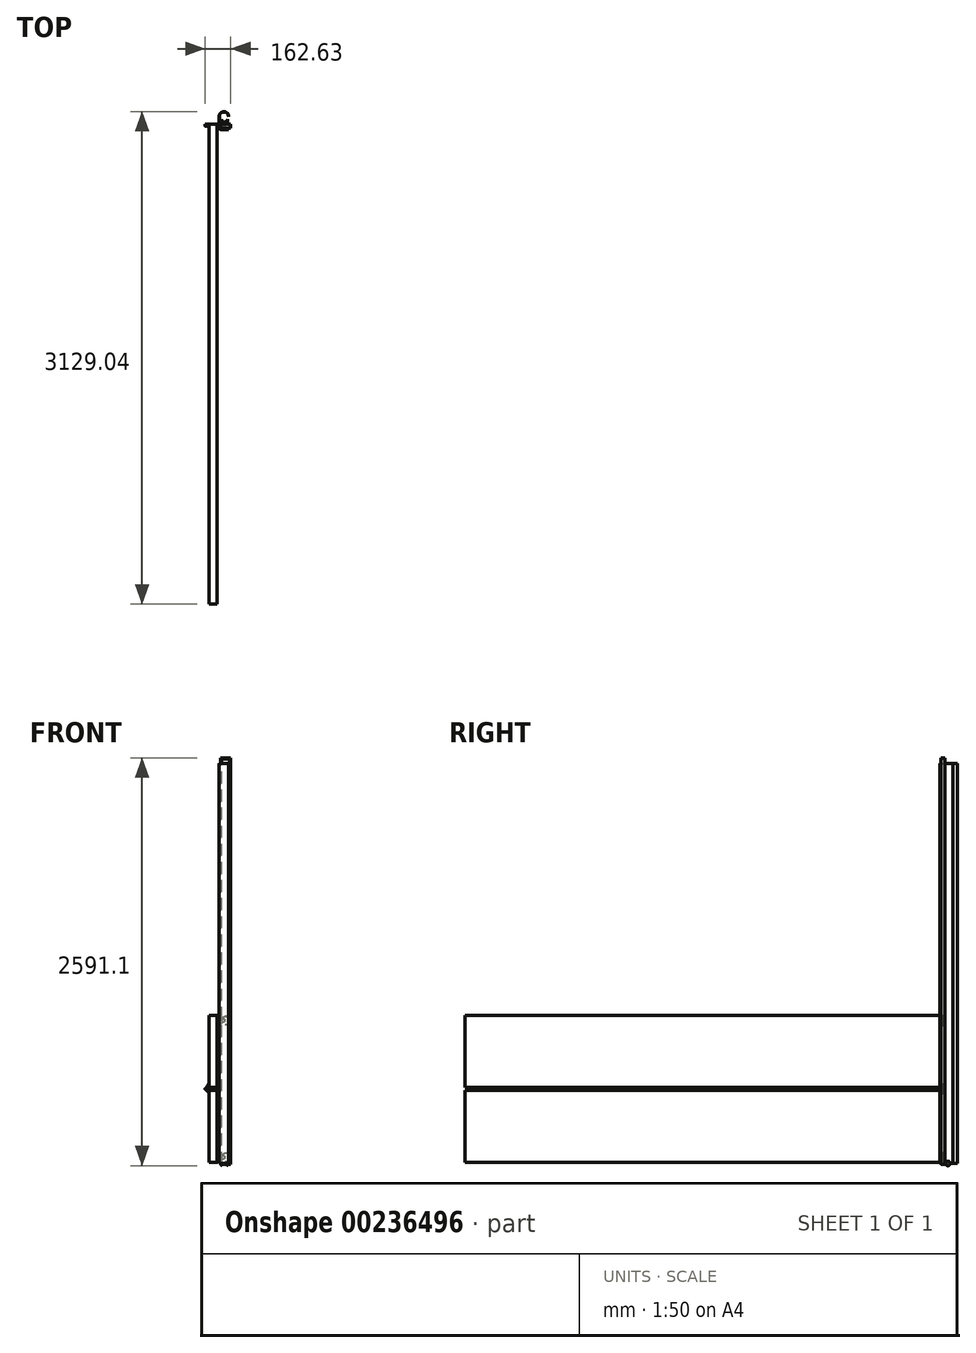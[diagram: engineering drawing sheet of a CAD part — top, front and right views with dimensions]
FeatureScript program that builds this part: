
annotation { "Feature Type Name" : "Feature", "Feature Type Description" : "" }
export const myFeature = defineFeature(function(context is Context, id is Id, definition is map)
    precondition{}
    {
        {
            var Q0;
            Q0=qCreatedBy(makeId("Top.planeOp"),FACE);
            var sketch = newSketch(context, id + "F0", { "sketchPlane" : qUnion([Q0])});
            skLineSegment(sketch, "E0", {"start": v(-40.45, -23.65) * mm, "end": v(-40.45, 50.36) * mm});
            skArc(sketch, "E1", {"start": v(-40.45, 50.36) * mm, "mid": v(-11.8, 79) * mm, "end": v(16.83, 50.36) * mm});
            skLineSegment(sketch, "E2", {"start": v(-34.1, -30) * mm, "end": v(16.83, -30) * mm});
            skPoint(sketch, "E3.visualSharp", {"position": v(-40.45, -30) * mm});
            skArc(sketch, "E3.filletArc", {"start": v(-40.45, -23.65) * mm, "mid": v(-38.6, -28.14) * mm, "end": v(-34.1, -30) * mm});
            skArc(sketch, "E4.0", {"start": v(-42.49, 50.36) * mm, "mid": v(-11.8, 81.04) * mm, "end": v(18.87, 50.36) * mm});
            skLineSegment(sketch, "E4.1", {"start": v(-42.49, -23.65) * mm, "end": v(-42.49, 50.36) * mm});
            skArc(sketch, "E4.2", {"start": v(-42.49, -23.65) * mm, "mid": v(-40.03, -29.58) * mm, "end": v(-34.1, -32.03) * mm});
            skLineSegment(sketch, "E4.3", {"start": v(-34.1, -32.03) * mm, "end": v(16.83, -32.03) * mm});
            skLineSegment(sketch, "E5", {"start": v(16.83, 50.36) * mm, "end": v(18.87, 50.36) * mm});
            skLineSegment(sketch, "E6", {"start": v(16.83, -30) * mm, "end": v(16.83, -32.03) * mm});
            skArc(sketch, "E7", {"start": v(11.06, 34.51) * mm, "mid": v(-8.2, 53.78) * mm, "end": v(-27.46, 34.51) * mm});
            skLineSegment(sketch, "E8", {"start": v(11.06, 34.51) * mm, "end": v(11.06, 20.4) * mm});
            skLineSegment(sketch, "E9", {"start": v(-27.46, 34.51) * mm, "end": v(-27.46, 20.4) * mm});
            skLineSegment(sketch, "E10", {"start": v(-27.46, 20.4) * mm, "end": v(11.06, 20.4) * mm});
            skSolve(sketch);
        }
        {
            var Q0;
            Q0=makeQuery(id+"F0.imprint","IMPRINT",FACE,{"disambiguationData":[TD([[makeQuery(id+"F0.imprint","IMPRINT",EDGE,{"derivedFrom":sQuery(id+"F0.wireOp",EDGE,"E0")}),1.0]])]});
            extrude(context, id + "F1", {"entities" : qUnion([Q0]), "depth" : 2540 * mm});
        }
        {
            var Q0;
            Q0=makeQuery(id+"F0.imprint","IMPRINT",FACE,{"disambiguationData":[TD([[makeQuery(id+"F0.imprint","IMPRINT",EDGE,{"derivedFrom":sQuery(id+"F0.wireOp",EDGE,"E7")}),1.0]])]});
            var Q1;
            Q1=sQuery(id+"F0.wireOp",EDGE,"E10");
            revolve(context, id + "F2", {"entities" : qUnion([Q0]), "axis" : qUnion([Q1]), "revolveType" : RevolveType.FULL});
        }
        {
            var Q0;
            Q0=qCreatedBy(makeId("Front.planeOp"),FACE);
            var sketch = newSketch(context, id + "F3", { "sketchPlane" : qUnion([Q0])});
            skLineSegment(sketch, "E11.bottom", {"start": v(-105.8, 463.81) * mm, "end": v(-55, 463.81) * mm});
            skLineSegment(sketch, "E11.top", {"start": v(-105.8, 6.61) * mm, "end": v(-55, 6.61) * mm});
            skLineSegment(sketch, "E11.left", {"start": v(-105.8, 463.81) * mm, "end": v(-105.8, 6.61) * mm});
            skLineSegment(sketch, "E11.right", {"start": v(-55, 463.81) * mm, "end": v(-55, 6.61) * mm});
            skLineSegment(sketch, "E12.bottom", {"start": v(-415.45, 758.42) * mm, "end": v(-364.65, 758.42) * mm});
            skLineSegment(sketch, "E12.top", {"start": v(-415.45, 301.22) * mm, "end": v(-364.65, 301.22) * mm});
            skLineSegment(sketch, "E12.left", {"start": v(-415.45, 758.42) * mm, "end": v(-415.45, 301.22) * mm});
            skLineSegment(sketch, "E12.right", {"start": v(-364.65, 758.42) * mm, "end": v(-364.65, 301.22) * mm});
            skCircle(sketch, "E13", {"center": v(0, 38.36) * mm, "radius": 25.4 * mm});
            skLineSegment(sketch, "E14.bottom", {"start": v(-25.4, 0) * mm, "end": v(25.4, 0) * mm});
            skLineSegment(sketch, "E14.top", {"start": v(-25.4, 2570.64) * mm, "end": v(25.4, 2570.64) * mm});
            skLineSegment(sketch, "E14.left", {"start": v(-25.4, 0) * mm, "end": v(-25.4, 2570.64) * mm});
            skLineSegment(sketch, "E14.right", {"start": v(25.4, 0) * mm, "end": v(25.4, 2570.64) * mm});
            skLineSegment(sketch, "E15", {"start": v(0, 0) * mm, "end": v(0, 2570.64) * mm, "construction": true});
            skLineSegment(sketch, "E16.0", {"start": v(31.75, -6.35) * mm, "end": v(31.75, 2576.99) * mm});
            skLineSegment(sketch, "E16.1", {"start": v(-31.75, -6.35) * mm, "end": v(31.75, -6.35) * mm});
            skLineSegment(sketch, "E16.2", {"start": v(-31.75, -6.35) * mm, "end": v(-31.75, 2576.99) * mm});
            skLineSegment(sketch, "E16.3", {"start": v(-31.75, 2576.99) * mm, "end": v(31.75, 2576.99) * mm});
            skCircle(sketch, "E17", {"center": v(147, 574.1) * mm, "radius": 25.4 * mm});
            skLineSegment(sketch, "E18.bottom", {"start": v(121.6, 6.35) * mm, "end": v(172.4, 6.35) * mm});
            skLineSegment(sketch, "E18.top", {"start": v(121.6, 2576.99) * mm, "end": v(172.4, 2576.99) * mm});
            skLineSegment(sketch, "E18.left", {"start": v(121.6, 6.35) * mm, "end": v(121.6, 2576.99) * mm});
            skLineSegment(sketch, "E18.right", {"start": v(172.4, 6.35) * mm, "end": v(172.4, 2576.99) * mm});
            skLineSegment(sketch, "E19", {"start": v(147, 6.35) * mm, "end": v(147, 2576.99) * mm, "construction": true});
            skLineSegment(sketch, "E20.0", {"start": v(178.74, 0) * mm, "end": v(178.74, 2583.34) * mm});
            skLineSegment(sketch, "E20.1", {"start": v(115.24, 0) * mm, "end": v(178.74, 0) * mm});
            skLineSegment(sketch, "E20.2", {"start": v(115.24, 0) * mm, "end": v(115.24, 2583.34) * mm});
            skLineSegment(sketch, "E20.3", {"start": v(115.24, 2583.34) * mm, "end": v(178.74, 2583.34) * mm});
            skLineSegment(sketch, "E21", {"start": v(-55, 6.61) * mm, "end": v(0, 38.36) * mm});
            skLineSegment(sketch, "E22", {"start": v(0, 38.36) * mm, "end": v(-55, 70.11) * mm});
            skLineSegment(sketch, "E23.bottom", {"start": v(-105.8, 939.06) * mm, "end": v(-55, 939.06) * mm});
            skLineSegment(sketch, "E23.left", {"start": v(-105.8, 939.06) * mm, "end": v(-105.8, 481.86) * mm});
            skLineSegment(sketch, "E23.right", {"start": v(-55, 939.06) * mm, "end": v(-55, 481.86) * mm});
            skCircle(sketch, "E24", {"center": v(0, 907.3) * mm, "radius": 25.4 * mm});
            skLineSegment(sketch, "E25", {"start": v(-55, 875.56) * mm, "end": v(0, 907.3) * mm});
            skLineSegment(sketch, "E26", {"start": v(0, 907.3) * mm, "end": v(-55, 939.06) * mm});
            skLineSegment(sketch, "E27", {"start": v(-55, 481.86) * mm, "end": v(-105.8, 481.86) * mm});
            skCircle(sketch, "E28", {"center": v(-124.71, 473.3) * mm, "radius": 6.17 * mm});
            skLineSegment(sketch, "E29", {"start": v(-124.71, 473.3) * mm, "end": v(-105.8, 481.86) * mm});
            skLineSegment(sketch, "E30", {"start": v(-124.71, 473.3) * mm, "end": v(-105.8, 463.81) * mm});
            skLineSegment(sketch, "E31", {"start": v(-124.71, 473.3) * mm, "end": v(-105.8, 504.05) * mm});
            skLineSegment(sketch, "E32", {"start": v(-105.8, 504.05) * mm, "end": v(-124.71, 473.3) * mm});
            skLineSegment(sketch, "E33", {"start": v(-124.71, 473.3) * mm, "end": v(-105.8, 443.96) * mm});
            skSolve(sketch);
        }
        {
            var Q0;
            {var subQ0=sQuery(id+"F3.wireOp",EDGE,"E22");var subQ1=sQuery(id+"F3.wireOp",EDGE,"E14.left");var subQ2=makeQuery(id+"F3.imprint","INTERSECT",VERTEX,{"derivedFrom":[subQ1,subQ0]});Q0=makeQuery(id+"F3.imprint","IMPRINT",FACE,{"disambiguationData":[TD([[makeQuery(id+"F3.imprint","IMPRINT",EDGE,{"disambiguationData":[TD([[subQ2,-1.0]])],"derivedFrom":subQ1}),1.0]])]});}
            var Q1;
            {var subQ5=sQuery(id+"F3.wireOp",EDGE,"E14.left");var subQ6=makeQuery(id+"F3.imprint","INTERSECT",VERTEX,{"derivedFrom":[sQuery(id+"F3.wireOp",EDGE,"E13"),subQ5]});Q1=makeQuery(id+"F3.imprint","IMPRINT",FACE,{"disambiguationData":[TD([[makeQuery(id+"F3.imprint","IMPRINT",EDGE,{"disambiguationData":[TD([[subQ6,1.0]])],"derivedFrom":subQ5}),1.0]])]});}
            var Q2;
            {var subQ9=sQuery(id+"F3.wireOp",EDGE,"E14.bottom");Q2=makeQuery(id+"F3.imprint","IMPRINT",FACE,{"disambiguationData":[TD([[makeQuery(id+"F3.imprint","IMPRINT",EDGE,{"derivedFrom":subQ9}),-1.0]])]});}
            var Q3;
            {var subQ0=sQuery(id+"F3.wireOp",EDGE,"E25");var subQ1=sQuery(id+"F3.wireOp",EDGE,"E14.left");var subQ2=makeQuery(id+"F3.imprint","INTERSECT",VERTEX,{"derivedFrom":[subQ1,subQ0]});Q3=makeQuery(id+"F3.imprint","IMPRINT",FACE,{"disambiguationData":[TD([[makeQuery(id+"F3.imprint","IMPRINT",EDGE,{"disambiguationData":[TD([[subQ2,-1.0]])],"derivedFrom":subQ1}),1.0]])]});}
            extrude(context, id + "F4", {"entities" : qUnion([Q0, Q1, Q2, Q3]), "depth" : 25.4 * mm});
        }
        {
            var Q0;
            {var subQ0=sQuery(id+"F3.wireOp",EDGE,"E24");var subQ1=makeQuery(id+"F3.imprint","INTERSECT",VERTEX,{"derivedFrom":[sQuery(id+"F3.wireOp",EDGE,"E14.right"),subQ0]});Q0=makeQuery(id+"F3.imprint","IMPRINT",FACE,{"disambiguationData":[TD([[makeQuery(id+"F3.imprint","IMPRINT",EDGE,{"disambiguationData":[TD([[subQ1,-1.0]])],"derivedFrom":subQ0}),1.0]])]});}
            var Q1;
            {var subQ0=sQuery(id+"F3.wireOp",EDGE,"E24");var subQ1=makeQuery(id+"F3.imprint","INTERSECT",VERTEX,{"derivedFrom":[sQuery(id+"F3.wireOp",EDGE,"E14.left"),subQ0]});Q1=makeQuery(id+"F3.imprint","IMPRINT",FACE,{"disambiguationData":[TD([[makeQuery(id+"F3.imprint","IMPRINT",EDGE,{"disambiguationData":[TD([[subQ1,1.0]])],"derivedFrom":subQ0}),1.0]])]});}
            var Q2;
            {var subQ0=sQuery(id+"F3.wireOp",EDGE,"E22");var subQ1=sQuery(id+"F3.wireOp",EDGE,"E13");var subQ2=makeQuery(id+"F3.imprint","INTERSECT",VERTEX,{"derivedFrom":[subQ1,subQ0]});Q2=makeQuery(id+"F3.imprint","IMPRINT",FACE,{"disambiguationData":[TD([[makeQuery(id+"F3.imprint","IMPRINT",EDGE,{"disambiguationData":[TD([[subQ2,1.0]])],"derivedFrom":subQ1}),1.0]])]});}
            var Q3;
            {var subQ0=sQuery(id+"F3.wireOp",EDGE,"E22");var subQ1=sQuery(id+"F3.wireOp",EDGE,"E13");var subQ2=makeQuery(id+"F3.imprint","INTERSECT",VERTEX,{"derivedFrom":[subQ1,subQ0]});Q3=makeQuery(id+"F3.imprint","IMPRINT",FACE,{"disambiguationData":[TD([[makeQuery(id+"F3.imprint","IMPRINT",EDGE,{"disambiguationData":[TD([[subQ2,-1.0]])],"derivedFrom":subQ1}),1.0]])]});}
            extrude(context, id + "F5", {"entities" : qUnion([Q0, Q1, Q2, Q3]), "depth" : 25.4 * mm});
        }
        {
            var Q0;
            {var subQ3=sQuery(id+"F3.wireOp",EDGE,"E11.bottom");Q0=makeQuery(id+"F3.imprint","IMPRINT",FACE,{"disambiguationData":[TD([[makeQuery(id+"F3.imprint","IMPRINT",EDGE,{"derivedFrom":subQ3}),-1.0]])]});}
            var Q1;
            {var subQ1=sQuery(id+"F3.wireOp",EDGE,"E23.bottom");Q1=makeQuery(id+"F3.imprint","IMPRINT",FACE,{"disambiguationData":[TD([[makeQuery(id+"F3.imprint","IMPRINT",EDGE,{"derivedFrom":subQ1}),-1.0]])]});}
            extrude(context, id + "F6", {"entities" : qUnion([Q0, Q1]), "depth" : 3048 * mm});
        }
        {
            var Q0;
            {var subQ0=sQuery(id+"F3.wireOp",EDGE,"E21");var subQ5=sQuery(id+"F3.wireOp",EDGE,"E16.2");var subQ6=makeQuery(id+"F3.imprint","INTERSECT",VERTEX,{"derivedFrom":[subQ5,subQ0]});Q0=makeQuery(id+"F3.imprint","IMPRINT",FACE,{"disambiguationData":[TD([[makeQuery(id+"F3.imprint","IMPRINT",EDGE,{"disambiguationData":[TD([[subQ6,-1.0]])],"derivedFrom":subQ5}),1.0]])]});}
            var Q1;
            {var subQ5=sQuery(id+"F3.wireOp",EDGE,"E14.left");var subQ6=makeQuery(id+"F3.imprint","INTERSECT",VERTEX,{"derivedFrom":[sQuery(id+"F3.wireOp",EDGE,"E13"),subQ5]});Q1=makeQuery(id+"F3.imprint","IMPRINT",FACE,{"disambiguationData":[TD([[makeQuery(id+"F3.imprint","IMPRINT",EDGE,{"disambiguationData":[TD([[subQ6,1.0]])],"derivedFrom":subQ5}),1.0]])]});}
            var Q2;
            {var subQ0=sQuery(id+"F3.wireOp",EDGE,"E22");var subQ1=sQuery(id+"F3.wireOp",EDGE,"E13");var subQ2=makeQuery(id+"F3.imprint","INTERSECT",VERTEX,{"derivedFrom":[subQ1,subQ0]});Q2=makeQuery(id+"F3.imprint","IMPRINT",FACE,{"disambiguationData":[TD([[makeQuery(id+"F3.imprint","IMPRINT",EDGE,{"disambiguationData":[TD([[subQ2,-1.0]])],"derivedFrom":subQ1}),-1.0]])]});}
            var Q3;
            {var subQ0=sQuery(id+"F3.wireOp",EDGE,"E14.left");var subQ1=sQuery(id+"F3.wireOp",EDGE,"E13");var subQ2=makeQuery(id+"F3.imprint","INTERSECT",VERTEX,{"derivedFrom":[subQ1,subQ0]});Q3=makeQuery(id+"F3.imprint","IMPRINT",FACE,{"disambiguationData":[TD([[makeQuery(id+"F3.imprint","IMPRINT",EDGE,{"disambiguationData":[TD([[subQ2,-1.0]])],"derivedFrom":subQ1}),-1.0]])]});}
            var Q4;
            {var subQ0=sQuery(id+"F3.wireOp",EDGE,"E22");var subQ1=sQuery(id+"F3.wireOp",EDGE,"E13");var subQ2=makeQuery(id+"F3.imprint","INTERSECT",VERTEX,{"derivedFrom":[subQ1,subQ0]});Q4=makeQuery(id+"F3.imprint","IMPRINT",FACE,{"disambiguationData":[TD([[makeQuery(id+"F3.imprint","IMPRINT",EDGE,{"disambiguationData":[TD([[subQ2,-1.0]])],"derivedFrom":subQ1}),1.0]])]});}
            var Q5;
            {var subQ3=sQuery(id+"F3.wireOp",EDGE,"E33");var subQ5=sQuery(id+"F3.wireOp",EDGE,"E28");var subQ6=makeQuery(id+"F3.imprint","INTERSECT",VERTEX,{"derivedFrom":[subQ5,subQ3]});Q5=makeQuery(id+"F3.imprint","IMPRINT",FACE,{"disambiguationData":[TD([[makeQuery(id+"F3.imprint","IMPRINT",EDGE,{"disambiguationData":[TD([[subQ6,-1.0]])],"derivedFrom":subQ5}),-1.0]])]});}
            var Q6;
            {var subQ3=sQuery(id+"F3.wireOp",EDGE,"E32");var subQ5=sQuery(id+"F3.wireOp",EDGE,"E28");var subQ6=makeQuery(id+"F3.imprint","INTERSECT",VERTEX,{"derivedFrom":[subQ5,subQ3]});Q6=makeQuery(id+"F3.imprint","IMPRINT",FACE,{"disambiguationData":[TD([[makeQuery(id+"F3.imprint","IMPRINT",EDGE,{"disambiguationData":[TD([[subQ6,1.0]])],"derivedFrom":subQ5}),-1.0]])]});}
            var Q7;
            {var subQ0=sQuery(id+"F3.wireOp",EDGE,"E29");var subQ1=sQuery(id+"F3.wireOp",EDGE,"E28");var subQ2=makeQuery(id+"F3.imprint","INTERSECT",VERTEX,{"derivedFrom":[subQ1,subQ0]});Q7=makeQuery(id+"F3.imprint","IMPRINT",FACE,{"disambiguationData":[TD([[makeQuery(id+"F3.imprint","IMPRINT",EDGE,{"disambiguationData":[TD([[subQ2,1.0]])],"derivedFrom":subQ1}),1.0]])]});}
            var Q8;
            {var subQ0=sQuery(id+"F3.wireOp",EDGE,"E32");var subQ1=sQuery(id+"F3.wireOp",EDGE,"E28");var subQ2=makeQuery(id+"F3.imprint","INTERSECT",VERTEX,{"derivedFrom":[subQ1,subQ0]});Q8=makeQuery(id+"F3.imprint","IMPRINT",FACE,{"disambiguationData":[TD([[makeQuery(id+"F3.imprint","IMPRINT",EDGE,{"disambiguationData":[TD([[subQ2,-1.0]])],"derivedFrom":subQ1}),1.0]])]});}
            var Q9;
            {var subQ0=sQuery(id+"F3.wireOp",EDGE,"E32");var subQ1=sQuery(id+"F3.wireOp",EDGE,"E28");var subQ2=makeQuery(id+"F3.imprint","INTERSECT",VERTEX,{"derivedFrom":[subQ1,subQ0]});Q9=makeQuery(id+"F3.imprint","IMPRINT",FACE,{"disambiguationData":[TD([[makeQuery(id+"F3.imprint","IMPRINT",EDGE,{"disambiguationData":[TD([[subQ2,1.0]])],"derivedFrom":subQ1}),1.0]])]});}
            var Q10;
            {var subQ0=sQuery(id+"F3.wireOp",EDGE,"E33");var subQ1=sQuery(id+"F3.wireOp",EDGE,"E28");var subQ2=makeQuery(id+"F3.imprint","INTERSECT",VERTEX,{"derivedFrom":[subQ1,subQ0]});Q10=makeQuery(id+"F3.imprint","IMPRINT",FACE,{"disambiguationData":[TD([[makeQuery(id+"F3.imprint","IMPRINT",EDGE,{"disambiguationData":[TD([[subQ2,-1.0]])],"derivedFrom":subQ1}),1.0]])]});}
            var Q11;
            {var subQ0=sQuery(id+"F3.wireOp",EDGE,"E26");var subQ1=sQuery(id+"F3.wireOp",EDGE,"E16.2");var subQ2=makeQuery(id+"F3.imprint","INTERSECT",VERTEX,{"derivedFrom":[subQ1,subQ0]});Q11=makeQuery(id+"F3.imprint","IMPRINT",FACE,{"disambiguationData":[TD([[makeQuery(id+"F3.imprint","IMPRINT",EDGE,{"disambiguationData":[TD([[subQ2,1.0]])],"derivedFrom":subQ1}),1.0]])]});}
            var Q12;
            {var subQ0=sQuery(id+"F3.wireOp",EDGE,"E25");var subQ1=sQuery(id+"F3.wireOp",EDGE,"E14.left");var subQ2=makeQuery(id+"F3.imprint","INTERSECT",VERTEX,{"derivedFrom":[subQ1,subQ0]});Q12=makeQuery(id+"F3.imprint","IMPRINT",FACE,{"disambiguationData":[TD([[makeQuery(id+"F3.imprint","IMPRINT",EDGE,{"disambiguationData":[TD([[subQ2,-1.0]])],"derivedFrom":subQ1}),1.0]])]});}
            var Q13;
            {var subQ0=sQuery(id+"F3.wireOp",EDGE,"E24");var subQ1=makeQuery(id+"F3.imprint","INTERSECT",VERTEX,{"derivedFrom":[sQuery(id+"F3.wireOp",EDGE,"E14.left"),subQ0]});Q13=makeQuery(id+"F3.imprint","IMPRINT",FACE,{"disambiguationData":[TD([[makeQuery(id+"F3.imprint","IMPRINT",EDGE,{"disambiguationData":[TD([[subQ1,1.0]])],"derivedFrom":subQ0}),1.0]])]});}
            var Q14;
            {var subQ0=sQuery(id+"F3.wireOp",EDGE,"E24");var subQ1=sQuery(id+"F3.wireOp",EDGE,"E14.left");var subQ2=makeQuery(id+"F3.imprint","INTERSECT",VERTEX,{"derivedFrom":[subQ1,subQ0]});Q14=makeQuery(id+"F3.imprint","IMPRINT",FACE,{"disambiguationData":[TD([[makeQuery(id+"F3.imprint","IMPRINT",EDGE,{"disambiguationData":[TD([[subQ2,-1.0]])],"derivedFrom":subQ1}),-1.0]])]});}
            var Q15;
            {var subQ0=sQuery(id+"F3.wireOp",EDGE,"E25");var subQ1=sQuery(id+"F3.wireOp",EDGE,"E14.left");var subQ2=makeQuery(id+"F3.imprint","INTERSECT",VERTEX,{"derivedFrom":[subQ1,subQ0]});Q15=makeQuery(id+"F3.imprint","IMPRINT",FACE,{"disambiguationData":[TD([[makeQuery(id+"F3.imprint","IMPRINT",EDGE,{"disambiguationData":[TD([[subQ2,-1.0]])],"derivedFrom":subQ1}),-1.0]])]});}
            extrude(context, id + "F7", {"entities" : qUnion([Q0, Q1, Q2, Q3, Q4, Q5, Q6, Q7, Q8, Q9, Q10, Q11, Q12, Q13, Q14, Q15]), "depth" : 12.7 * mm});
        }
    });
